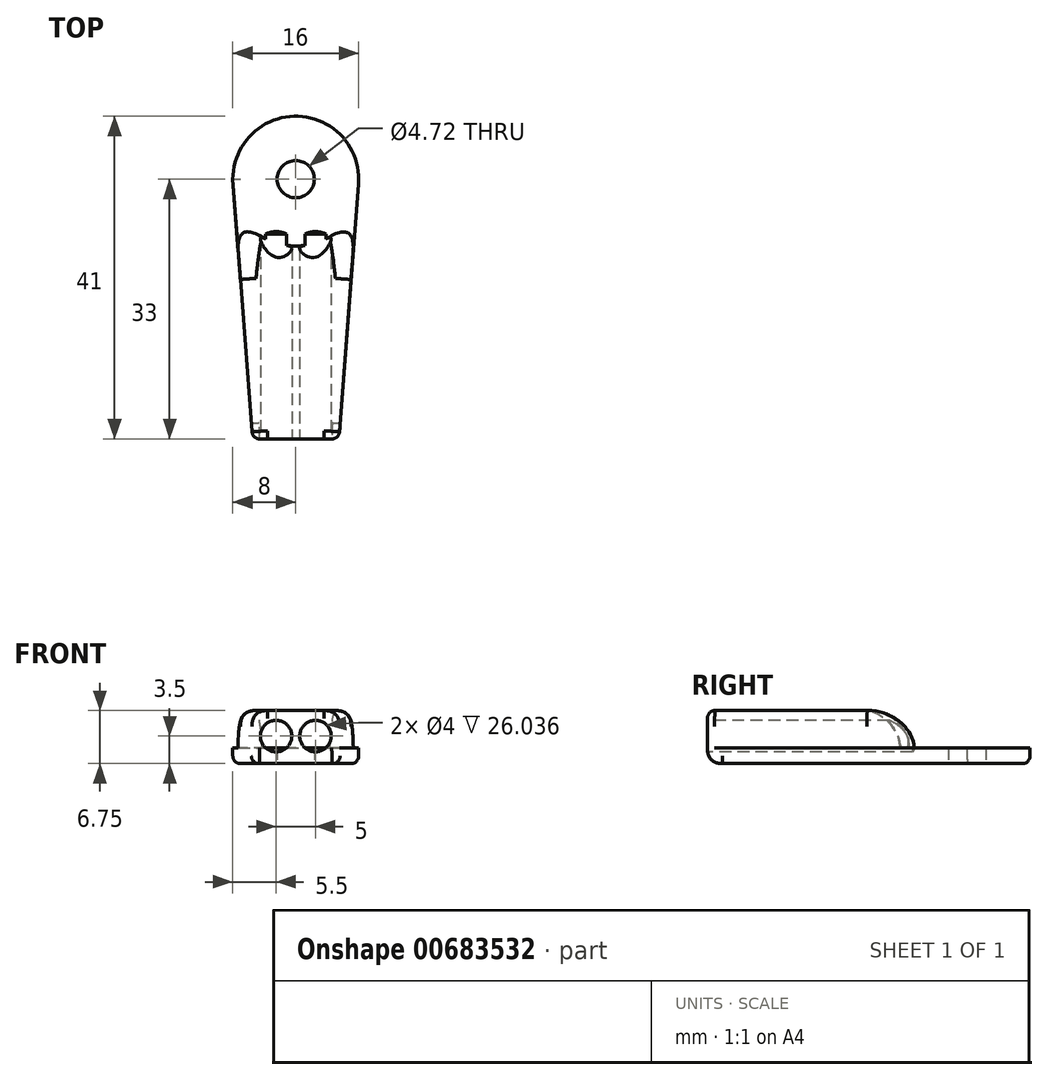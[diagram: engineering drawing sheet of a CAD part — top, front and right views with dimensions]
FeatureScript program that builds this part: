
annotation { "Feature Type Name" : "Feature", "Feature Type Description" : "" }
export const myFeature = defineFeature(function(context is Context, id is Id, definition is map)
    precondition{}
    {
        {
            var Q0;
            Q0=qCreatedBy(makeId("Top.planeOp"),FACE);
            var sketch = newSketch(context, id + "F0", { "sketchPlane" : qUnion([Q0])});
            skCircle(sketch, "E0", {"center": v(0, 0) * mm, "radius": 8 * mm});
            skLineSegment(sketch, "E1", {"start": v(-8, 0) * mm, "end": v(-5.5, -33) * mm});
            skLineSegment(sketch, "E2", {"start": v(-5.5, -33) * mm, "end": v(5.5, -33) * mm});
            skLineSegment(sketch, "E3", {"start": v(5.5, -33) * mm, "end": v(8.02, 0) * mm});
            skLineSegment(sketch, "E4", {"start": v(8.02, 0) * mm, "end": v(-8, 0) * mm});
            skCircle(sketch, "E5", {"center": v(0, 0) * mm, "radius": 2.36 * mm});
            skSolve(sketch);
        }
        {
            var Q0;
            {var subQ5=sQuery(id+"F0.wireOp",EDGE,"E2");Q0=makeQuery(id+"F0.imprint","IMPRINT",FACE,{"disambiguationData":[TD([[makeQuery(id+"F0.imprint","IMPRINT",EDGE,{"derivedFrom":subQ5}),1.0]])]});}
            var Q1;
            {var subQ0=sQuery(id+"F0.wireOp",EDGE,"E1");var subQ1=sQuery(id+"F0.wireOp",EDGE,"E0");var subQ2=makeQuery(id+"F0.imprint","INTERSECT",VERTEX,{"derivedFrom":[subQ1,subQ0]});Q1=makeQuery(id+"F0.imprint","IMPRINT",FACE,{"disambiguationData":[TD([[makeQuery(id+"F0.imprint","IMPRINT",EDGE,{"disambiguationData":[TD([[subQ2,-1.0]])],"derivedFrom":subQ1}),1.0]])]});}
            var Q2;
            {var subQ0=sQuery(id+"F0.wireOp",EDGE,"E4");var subQ1=sQuery(id+"F0.wireOp",EDGE,"E0");var subQ3=makeQuery(id+"F0.imprint","INTERSECT",VERTEX,{"derivedFrom":[subQ1,subQ0]});Q2=makeQuery(id+"F0.imprint","IMPRINT",FACE,{"disambiguationData":[TD([[makeQuery(id+"F0.imprint","IMPRINT",EDGE,{"disambiguationData":[TD([[subQ3,-1.0]])],"derivedFrom":subQ1}),1.0]])]});}
            extrude(context, id + "F1", {"entities" : qUnion([Q0, Q1, Q2]), "depth" : 2 * mm, "offsetDistance" : 25.4 * mm});
        }
        {
            var Q0;
            Q0=makeQuery(id+"F1.opExtrude","CAP_FACE",FACE,{"disambiguationData":[OSD([sQuery(id+"F0.wireOp",EDGE,"E0"),sQuery(id+"F0.wireOp",EDGE,"E1"),sQuery(id+"F0.wireOp",EDGE,"E2"),sQuery(id+"F0.wireOp",EDGE,"E3")])],"isStart":false});
            var sketch = newSketch(context, id + "F2", { "sketchPlane" : qUnion([Q0])});
            skCircle(sketch, "E6", {"center": v(0, 0) * mm, "radius": 6.95 * mm});
            skLineSegment(sketch, "E7", {"start": v(-8, 0) * mm, "end": v(-5.5, -33) * mm});
            skLineSegment(sketch, "E8", {"start": v(-5.5, -33) * mm, "end": v(5.5, -33) * mm});
            skLineSegment(sketch, "E9", {"start": v(5.5, -33) * mm, "end": v(7.98, 0) * mm});
            skLineSegment(sketch, "E10", {"start": v(7.98, 0) * mm, "end": v(-8, 0) * mm});
            skCircle(sketch, "E11", {"center": v(0, 0) * mm, "radius": 8.5 * mm});
            skSolve(sketch);
        }
        {
            var Q0;
            {var subQ5=sQuery(id+"F2.wireOp",EDGE,"E8");Q0=makeQuery(id+"F2.imprint","IMPRINT",FACE,{"disambiguationData":[TD([[makeQuery(id+"F2.imprint","IMPRINT",EDGE,{"derivedFrom":subQ5}),1.0]])]});}
            extrude(context, id + "F3", {"entities" : qUnion([Q0]), "operationType" : NewBodyOperationType.ADD, "depth" : (7.75 - 3) * mm, "offsetDistance" : 25.4 * mm});
        }
        {
            var Q0;
            Q0=makeQuery(id+"F3.opExtrude","CAP_EDGE",EDGE,{"disambiguationData":[OSD([sQuery(id+"F2.wireOp",EDGE,"E11")])],"isStart":false});
            fillet(context, id + "F4", {"entities" : qUnion([Q0]), "radius" : 5.08 * mm, "tangentPropagation" : true, "allowEdgeOverflow" : false});
        }
        {
            var Q0;
            Q0=makeQuery(id+"F1.opExtrude","CAP_EDGE",EDGE,{"disambiguationData":[OSD([sQuery(id+"F0.wireOp",EDGE,"E2")])],"isStart":true});
            fillet(context, id + "F5", {"entities" : qUnion([Q0]), "radius" : 2 * mm, "tangentPropagation" : true, "rho" : 0.5, "crossSection" : FilletCrossSection.CONIC, "allowEdgeOverflow" : false});
        }
        {
            var Q0;
            Q0=makeQuery(id+"F3.opExtrude","CAP_EDGE",EDGE,{"disambiguationData":[OSD([sQuery(id+"F2.wireOp",EDGE,"E9")])],"isStart":false});
            var Q1;
            Q1=makeQuery(id+"F3.opExtrude","CAP_EDGE",EDGE,{"disambiguationData":[OSD([sQuery(id+"F2.wireOp",EDGE,"E7")])],"isStart":false});
            fillet(context, id + "F6", {"entities" : qUnion([Q0, Q1]), "radius" : 2 * mm, "tangentPropagation" : true, "rho" : 0.5, "crossSection" : FilletCrossSection.CONIC, "allowEdgeOverflow" : false});
        }
        {
            var Q0;
            Q0=makeQuery(id+"F3.boolean.opBoolean","MERGE",FACE,{"derivedFrom":[makeQuery(id+"F1.opExtrude","SWEPT_FACE",FACE,{"disambiguationData":[OSD([sQuery(id+"F0.wireOp",EDGE,"E2")])]}),makeQuery(id+"F3.opExtrude","SWEPT_FACE",FACE,{"disambiguationData":[OSD([sQuery(id+"F2.wireOp",EDGE,"E8")])]})]});
            var sketch = newSketch(context, id + "F7", { "sketchPlane" : qUnion([Q0])});
            skLineSegment(sketch, "E12", {"start": v(0, 0) * mm, "end": v(0, 3.5) * mm});
            skLineSegment(sketch, "E13", {"start": v(0, 3.5) * mm, "end": v(2.5, 3.5) * mm});
            skLineSegment(sketch, "E14", {"start": v(0, 3.5) * mm, "end": v(-2.5, 3.5) * mm});
            skSolve(sketch);
        }
        {
            var Q0;
            Q0=sQuery(id+"F7.wireOp",VERTEX,"E14.end");
            var Q1;
            Q1=sQuery(id+"F7.wireOp",VERTEX,"E13.end");
            var Q2;
            Q2=makeQuery(id+"F1.opExtrude","SWEPT_BODY",BODY,{"disambiguationData":[OSD([sQuery(id+"F0.wireOp",EDGE,"E0"),sQuery(id+"F0.wireOp",EDGE,"E1"),sQuery(id+"F0.wireOp",EDGE,"E2"),sQuery(id+"F0.wireOp",EDGE,"E3"),sQuery(id+"F0.wireOp",EDGE,"E5")])]});
            hole(context, id + "F8", {"style" : HoleStyle.SIMPLE, "endStyle" : HoleEndStyle.BLIND, "holeDiameter" : 4 * mm, "majorDiameter" : 6.35 * mm, "holeDepth" : 26 * mm, "isTappedThrough" : true, "tappedDepth" : 12.7 * mm, "tapClearance" : 3, "locations" : qUnion([Q0, Q1]), "scope" : qUnion([Q2])});
        }
        {
            var Q0;
            Q0=makeQuery(id+"F3.boolean.opBoolean","MERGE",EDGE,{"derivedFrom":[makeQuery(id+"F1.opExtrude","SWEPT_EDGE",EDGE,{"disambiguationData":[OSD([sQuery(id+"F0.wireOp",EDGE,"E1"),sQuery(id+"F0.wireOp",EDGE,"E2")])]}),makeQuery(id+"F3.opExtrude","SWEPT_EDGE",EDGE,{"disambiguationData":[OSD([sQuery(id+"F2.wireOp",EDGE,"E7"),sQuery(id+"F2.wireOp",EDGE,"E8")])]})]});
            fillet(context, id + "F9", {"entities" : qUnion([Q0]), "radius" : 1 * mm, "tangentPropagation" : true, "allowEdgeOverflow" : false});
        }
    });
